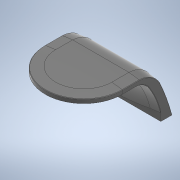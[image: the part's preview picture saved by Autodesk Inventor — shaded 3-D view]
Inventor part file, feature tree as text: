
AUTODESK INVENTOR PART (.ipt)
format: ipt  version: 2020 (Build 240168000, 168)  size: 7,305,728 bytes
history: native  units: in
note: dims shown in document units (in); Inventor stores cm internally (conversion verified against a paired STEP export)
features: chamfer x7, other x6, revolve x3, extrude x3, sketch x3, split x1, sweep x1
ambient origin geometry x8: Origin, YZ Plane, XZ Plane, XY Plane, X Axis, Y Axis, Z Axis, Center Point
bodies: Body1 (feature_tree)
feature tree (24):
  other  "ProfileTop"
  other  "ProfileSide"
  other  "XY_Project"
  other  "ProfileBack"
  revolve  "RevolvePlane"  [1 undecoded]
  revolve  "RevolveSketch"  [1 undecoded]
  extrude  "Extrusion5"  Depth=0.6693in
  extrude  "Extrusion6"  Depth=0.6693in
  split  "Split1"
  revolve  "Revolution1"  [1 undecoded]
  chamfer  "Chamfer4"  Distance=5.4528in
  chamfer  "Chamfer5"  Distance=2.937in
  chamfer  "Chamfer6"  Distance=16.7023in
  chamfer  "Chamfer7"  Distance=16.7023in
  sweep  "Sweep1"
  chamfer  "Chamfer8"  Distance=1.8504in
  chamfer  "Chamfer9"  Distance=7.4452in
  chamfer  "Chamfer10"  Distance=5.4724in
  other  "SensorDivet"
  extrude  "Extrusion7"  TaperAngle=0.0deg  [1 undecoded]
  other  "Image8"
  sketch  "Sketch9"  dims[d98=7.874in d109=2.278in]
  sketch  "3D Sketch1"
  sketch  "Sketch10"  dims[d110=12.4228in d111=3.715in d112=30.973in d142=7.874in d155=5.4528in d158=5.4528in d159=2.937in d160=16.7023in d161=16.7023in d162=2.937in d170=1.8504in d171=7.4452in d172=5.4724in d173=0.0in d174=4.9332in d175=5.4231in d176=1.7487in d177=4.8557in d178=1.8083in d179=1.6341in d180=0.8398in d181=0.0in d187=0.5906in d188=0.1969in d189=0.1969in d272=29.8893in d278=8.1496in d279=1.2598in d280=10.9449in d281=6.8898in d282=1.2598in d283=5.4724in d284=5.4724in d285=8.1496in d288=15.748in d289=0.0in d290=15.748in d291=0.0in d346=180.0deg d347=1.4961in d348=1.4961in d349=5.4724in d350=0.1969in d351=1.4961in d352=45.0deg d353=0.1969in d354=1.4961in d355=45.0deg d356=0.1969in d357=1.4961in d358=45.0deg d359=0.1969in d360=1.4961in d361=45.0deg d362=0.0in d363=0.0in d364=0.1969in d365=1.4961in d366=45.0deg d367=0.1969in d368=1.4961in d369=45.0deg d370=0.0591in d371=1.4961in d372=45.0deg d373=-1.9685in d375=0.0in d376=0.0in d377=1.4961in d378=1.4961in d379=0.0in d380=0.6693in d381=0.6693in d382=0.6693in d383=0.6693in d384=0.6693in d385=0.6693in d386=0.5512in d387=0.9055in d388=0.0in d163=0.0197in d164=0.0344in d165=0.0197in d166=0.0344in]
note: 4 required parameter values undecoded (feature->parameter linkage not recoverable at this tier; creation-order binding heuristic only, values carry confidence <= 0.55)